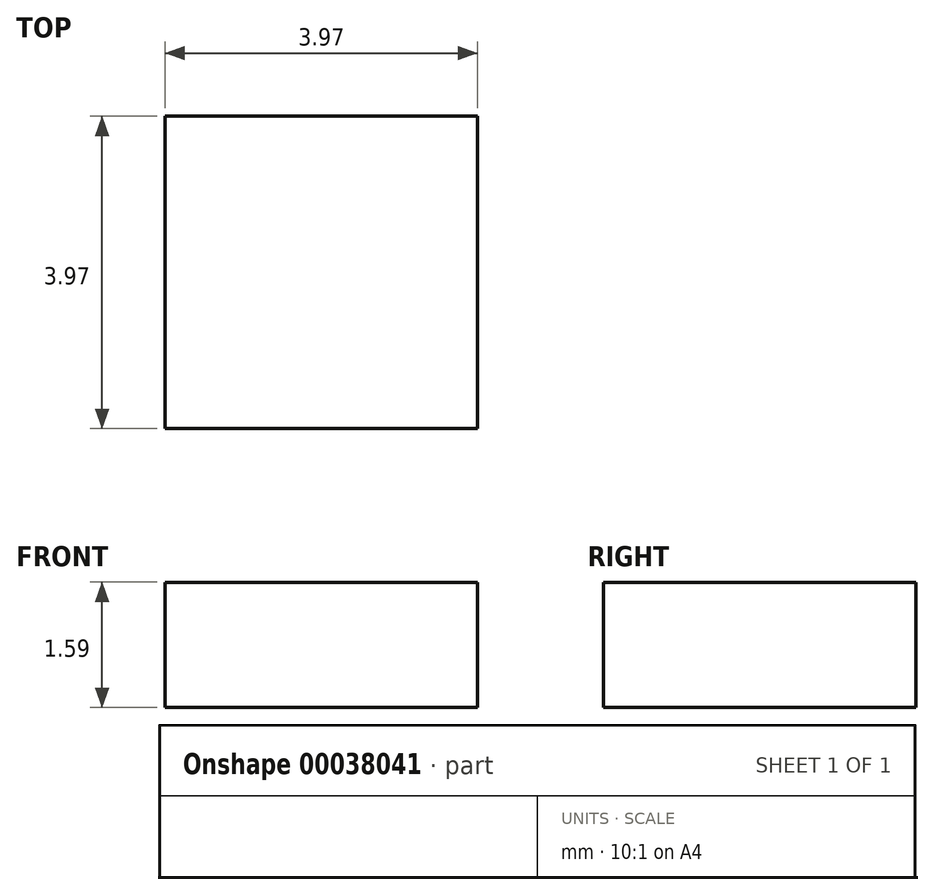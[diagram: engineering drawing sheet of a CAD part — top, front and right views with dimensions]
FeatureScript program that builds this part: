
annotation { "Feature Type Name" : "Feature", "Feature Type Description" : "" }
export const myFeature = defineFeature(function(context is Context, id is Id, definition is map)
    precondition{}
    {
        {
            var Q0;
            Q0=qCreatedBy(makeId("Top.planeOp"),FACE);
            var sketch = newSketch(context, id + "F0", { "sketchPlane" : qUnion([Q0])});
            skLineSegment(sketch, "E0.bottom", {"start": v(0, 0) * mm, "end": v(3.97, 0) * mm});
            skLineSegment(sketch, "E0.top", {"start": v(0, -3.97) * mm, "end": v(3.97, -3.97) * mm});
            skLineSegment(sketch, "E0.left", {"start": v(0, 0) * mm, "end": v(0, -3.97) * mm});
            skLineSegment(sketch, "E0.right", {"start": v(3.97, 0) * mm, "end": v(3.97, -3.97) * mm});
            skSolve(sketch);
        }
        {
            var Q0;
            Q0 = qSketchRegion(id + "F0", true);
            extrude(context, id + "F1", {"entities" : qUnion([Q0]), "depth" : 1.59 * mm});
        }
    });
